# Revit family: WCPan-FloorMounted-65cm-RimEx-CloseCoupled-Vitra-DlightSeries-9014B003-7200
name_source: partatom
category: Plumbing Fixtures
revit_build: Autodesk Revit 2017 (Build: 20160225_1515(x64)
units: mm (PartAtom-declared; Revit-internal decimal feet)

## family parameters
Cut with Voids When Loaded = No
Host = Face
OmniClass Number = 23.45.05.21.11
OmniClass Title = Water Closets
Part Type = Normal
Room Calculation Point = No
Round Connector Dimension = Use Diameter
Shared = Yes

## types (1)
- WCPan-FloorMounted-65cm-RimEx-CloseCoupled-Vitra-DlightSeries-9014B003-7200
    CW Connection = Yes
    Default Elevation = 400 mm  [stored 1.31234 ft]
    Description = WC Pan
    Manufacturer = VitrA
    Product Data URL = https://www.vitra-bad.fr
    URL = https://www.vitraglobal.com
    Waste Connection = Yes

note: [stored X ft] marks values corroborated as IEEE doubles in the binary element streams (Revit-internal decimal feet)

## geometry (parser evidence)
native form markers: Sweep x12
no freeform markers — native parametric forms only
